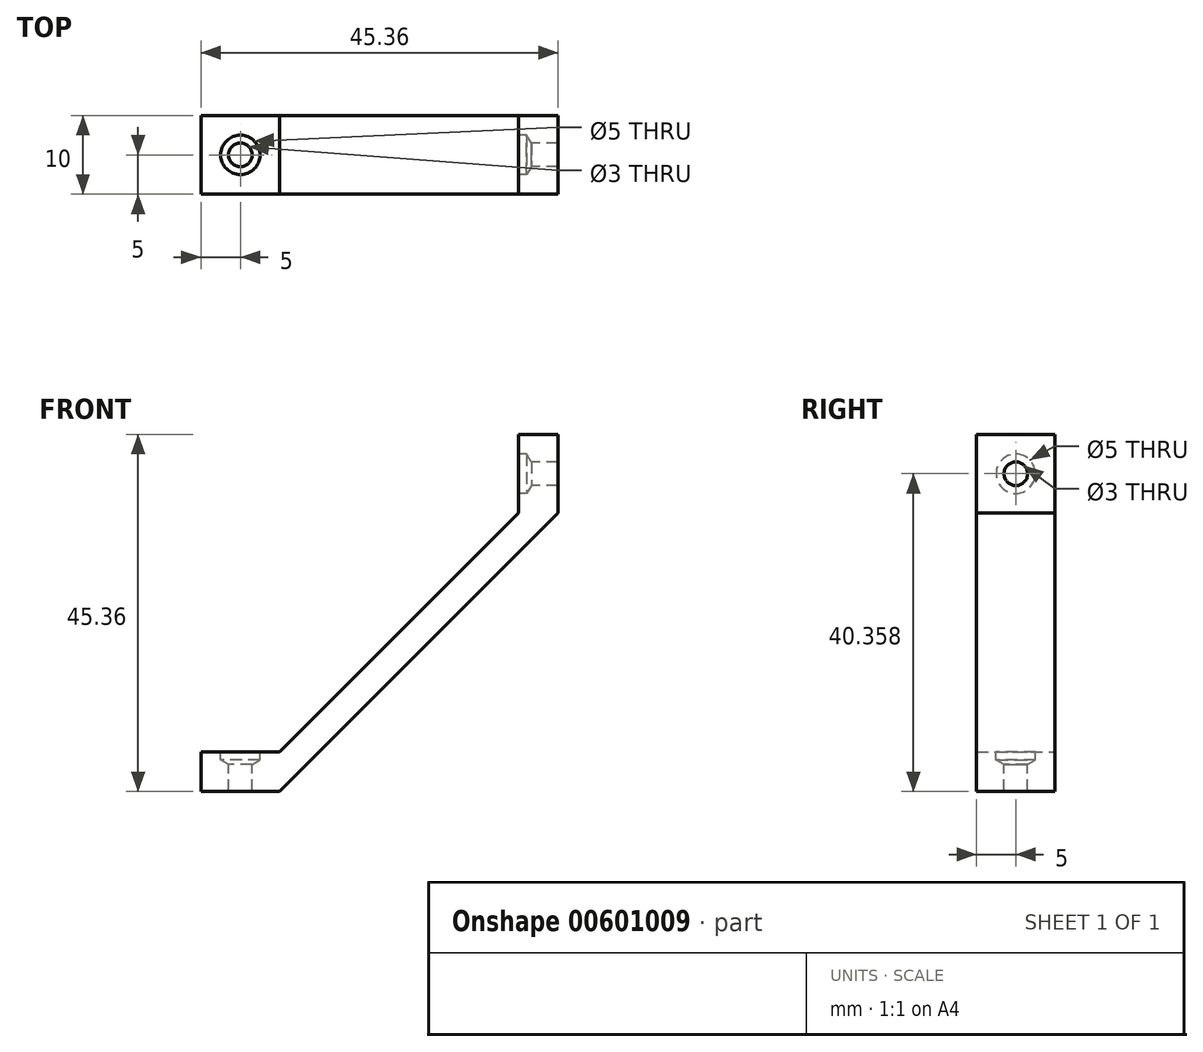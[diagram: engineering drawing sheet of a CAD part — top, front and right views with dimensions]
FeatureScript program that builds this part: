
annotation { "Feature Type Name" : "Feature", "Feature Type Description" : "" }
export const myFeature = defineFeature(function(context is Context, id is Id, definition is map)
    precondition{}
    {
        {
            var Q0;
            Q0=qCreatedBy(makeId("Front.planeOp"),FACE);
            var sketch = newSketch(context, id + "F0", { "sketchPlane" : qUnion([Q0])});
            skLineSegment(sketch, "E0", {"start": v(2.95, 53.36) * mm, "end": v(7.95, 53.36) * mm});
            skLineSegment(sketch, "E1", {"start": v(7.95, 43.36) * mm, "end": v(7.95, 53.36) * mm});
            skLineSegment(sketch, "E2", {"start": v(7.95, 43.36) * mm, "end": v(-27.4, 8) * mm});
            skLineSegment(sketch, "E3", {"start": v(-37.4, 8) * mm, "end": v(-27.4, 8) * mm});
            skLineSegment(sketch, "E4", {"start": v(-37.4, 8) * mm, "end": v(-37.4, 13) * mm});
            skLineSegment(sketch, "E5", {"start": v(-37.4, 13) * mm, "end": v(-27.4, 13) * mm});
            skLineSegment(sketch, "E6", {"start": v(-27.4, 13) * mm, "end": v(2.95, 43.36) * mm});
            skLineSegment(sketch, "E7", {"start": v(2.95, 43.36) * mm, "end": v(2.95, 53.36) * mm});
            skSolve(sketch);
        }
        {
            var Q0;
            Q0 = qSketchRegion(id + "F0", true);
            extrude(context, id + "F1", {"entities" : qUnion([Q0]), "depth" : 10 * mm, "offsetDistance" : 25 * mm});
        }
        {
            var Q0;
            Q0=makeQuery(id+"F1.opExtrude","SWEPT_FACE",FACE,{"disambiguationData":[OSD([sQuery(id+"F0.wireOp",EDGE,"E7")])]});
            var sketch = newSketch(context, id + "F2", { "sketchPlane" : qUnion([Q0])});
            skPoint(sketch, "E8.centerSnap0", {"position": v(10, 48.36) * mm});
            skCircle(sketch, "E9", {"center": v(5, 48.36) * mm, "radius": 1.5 * mm});
            skPoint(sketch, "E9.centerSnap0", {"position": v(5, 53.36) * mm});
            skCircle(sketch, "E10", {"center": v(0, 48.36) * mm, "radius": 0.48 * mm});
            skSolve(sketch);
        }
        {
            var Q0;
            Q0=sQuery(id+"F2.wireOp",VERTEX,"E9.center");
            var Q1;
            Q1=makeQuery(id+"F1.opExtrude","SWEPT_BODY",BODY,{"disambiguationData":[OSD([sQuery(id+"F0.wireOp",EDGE,"E0"),sQuery(id+"F0.wireOp",EDGE,"E1"),sQuery(id+"F0.wireOp",EDGE,"E2"),sQuery(id+"F0.wireOp",EDGE,"E3"),sQuery(id+"F0.wireOp",EDGE,"E4"),sQuery(id+"F0.wireOp",EDGE,"E5"),sQuery(id+"F0.wireOp",EDGE,"E6"),sQuery(id+"F0.wireOp",EDGE,"E7")])]});
            hole(context, id + "F3", {"style" : HoleStyle.SIMPLE, "endStyle" : HoleEndStyle.BLIND, "holeDiameter" : 5 * mm, "majorDiameter" : 5 * mm, "holeDepth" : 1 * mm, "isTappedThrough" : true, "tappedDepth" : 12 * mm, "tapClearance" : 3, "locations" : qUnion([Q0]), "scope" : qUnion([Q1])});
        }
        {
            var Q0;
            Q0=makeQuery(id+"F1.opExtrude","SWEPT_FACE",FACE,{"disambiguationData":[OSD([sQuery(id+"F0.wireOp",EDGE,"E5")])]});
            var sketch = newSketch(context, id + "F4", { "sketchPlane" : qUnion([Q0])});
            skCircle(sketch, "E11", {"center": v(-32.4, -5) * mm, "radius": 1.5 * mm});
            skPoint(sketch, "E11.centerSnap0", {"position": v(-37.4, -5) * mm});
            skPoint(sketch, "E11.centerSnap1", {"position": v(-32.4, 0) * mm});
            skSolve(sketch);
        }
        {
            var Q0;
            Q0=sQuery(id+"F4.wireOp",VERTEX,"E11.center");
            var Q1;
            Q1=makeQuery(id+"F1.opExtrude","SWEPT_BODY",BODY,{"disambiguationData":[OSD([sQuery(id+"F0.wireOp",EDGE,"E0"),sQuery(id+"F0.wireOp",EDGE,"E1"),sQuery(id+"F0.wireOp",EDGE,"E2"),sQuery(id+"F0.wireOp",EDGE,"E3"),sQuery(id+"F0.wireOp",EDGE,"E4"),sQuery(id+"F0.wireOp",EDGE,"E5"),sQuery(id+"F0.wireOp",EDGE,"E6"),sQuery(id+"F0.wireOp",EDGE,"E7")])]});
            hole(context, id + "F5", {"style" : HoleStyle.SIMPLE, "endStyle" : HoleEndStyle.BLIND, "holeDiameter" : 5 * mm, "majorDiameter" : 5 * mm, "holeDepth" : 1 * mm, "isTappedThrough" : true, "tappedDepth" : 12 * mm, "tapClearance" : 3, "locations" : qUnion([Q0]), "scope" : qUnion([Q1])});
        }
        {
            var Q0;
            Q0=makeQuery(id+"F1.opExtrude","SWEPT_FACE",FACE,{"disambiguationData":[OSD([sQuery(id+"F0.wireOp",EDGE,"E5")])]});
            var sketch = newSketch(context, id + "F6", { "sketchPlane" : qUnion([Q0])});
            skCircle(sketch, "E12", {"center": v(-32.4, -5) * mm, "radius": 1.5 * mm});
            skSolve(sketch);
        }
        {
            var Q0;
            Q0=sQuery(id+"F6.wireOp",VERTEX,"E12.center");
            var Q1;
            Q1=makeQuery(id+"F1.opExtrude","SWEPT_BODY",BODY,{"disambiguationData":[OSD([sQuery(id+"F0.wireOp",EDGE,"E0"),sQuery(id+"F0.wireOp",EDGE,"E1"),sQuery(id+"F0.wireOp",EDGE,"E2"),sQuery(id+"F0.wireOp",EDGE,"E3"),sQuery(id+"F0.wireOp",EDGE,"E4"),sQuery(id+"F0.wireOp",EDGE,"E5"),sQuery(id+"F0.wireOp",EDGE,"E6"),sQuery(id+"F0.wireOp",EDGE,"E7")])]});
            hole(context, id + "F7", {"style" : HoleStyle.SIMPLE, "endStyle" : HoleEndStyle.THROUGH, "holeDiameter" : 3 * mm, "majorDiameter" : 5 * mm, "isTappedThrough" : true, "tappedDepth" : 12 * mm, "tapClearance" : 3, "locations" : qUnion([Q0]), "scope" : qUnion([Q1])});
        }
        {
            var Q0;
            Q0=makeQuery(id+"F1.opExtrude","SWEPT_FACE",FACE,{"disambiguationData":[OSD([sQuery(id+"F0.wireOp",EDGE,"E7")])]});
            var sketch = newSketch(context, id + "F8", { "sketchPlane" : qUnion([Q0])});
            skCircle(sketch, "E13", {"center": v(5, 48.36) * mm, "radius": 1.5 * mm});
            skSolve(sketch);
        }
        {
            var Q0;
            Q0=sQuery(id+"F8.wireOp",VERTEX,"E13.center");
            var Q1;
            Q1=makeQuery(id+"F1.opExtrude","SWEPT_BODY",BODY,{"disambiguationData":[OSD([sQuery(id+"F0.wireOp",EDGE,"E0"),sQuery(id+"F0.wireOp",EDGE,"E1"),sQuery(id+"F0.wireOp",EDGE,"E2"),sQuery(id+"F0.wireOp",EDGE,"E3"),sQuery(id+"F0.wireOp",EDGE,"E4"),sQuery(id+"F0.wireOp",EDGE,"E5"),sQuery(id+"F0.wireOp",EDGE,"E6"),sQuery(id+"F0.wireOp",EDGE,"E7")])]});
            hole(context, id + "F9", {"style" : HoleStyle.SIMPLE, "endStyle" : HoleEndStyle.THROUGH, "holeDiameter" : 3 * mm, "majorDiameter" : 5 * mm, "isTappedThrough" : true, "tappedDepth" : 12 * mm, "tapClearance" : 3, "locations" : qUnion([Q0]), "scope" : qUnion([Q1])});
        }
    });
